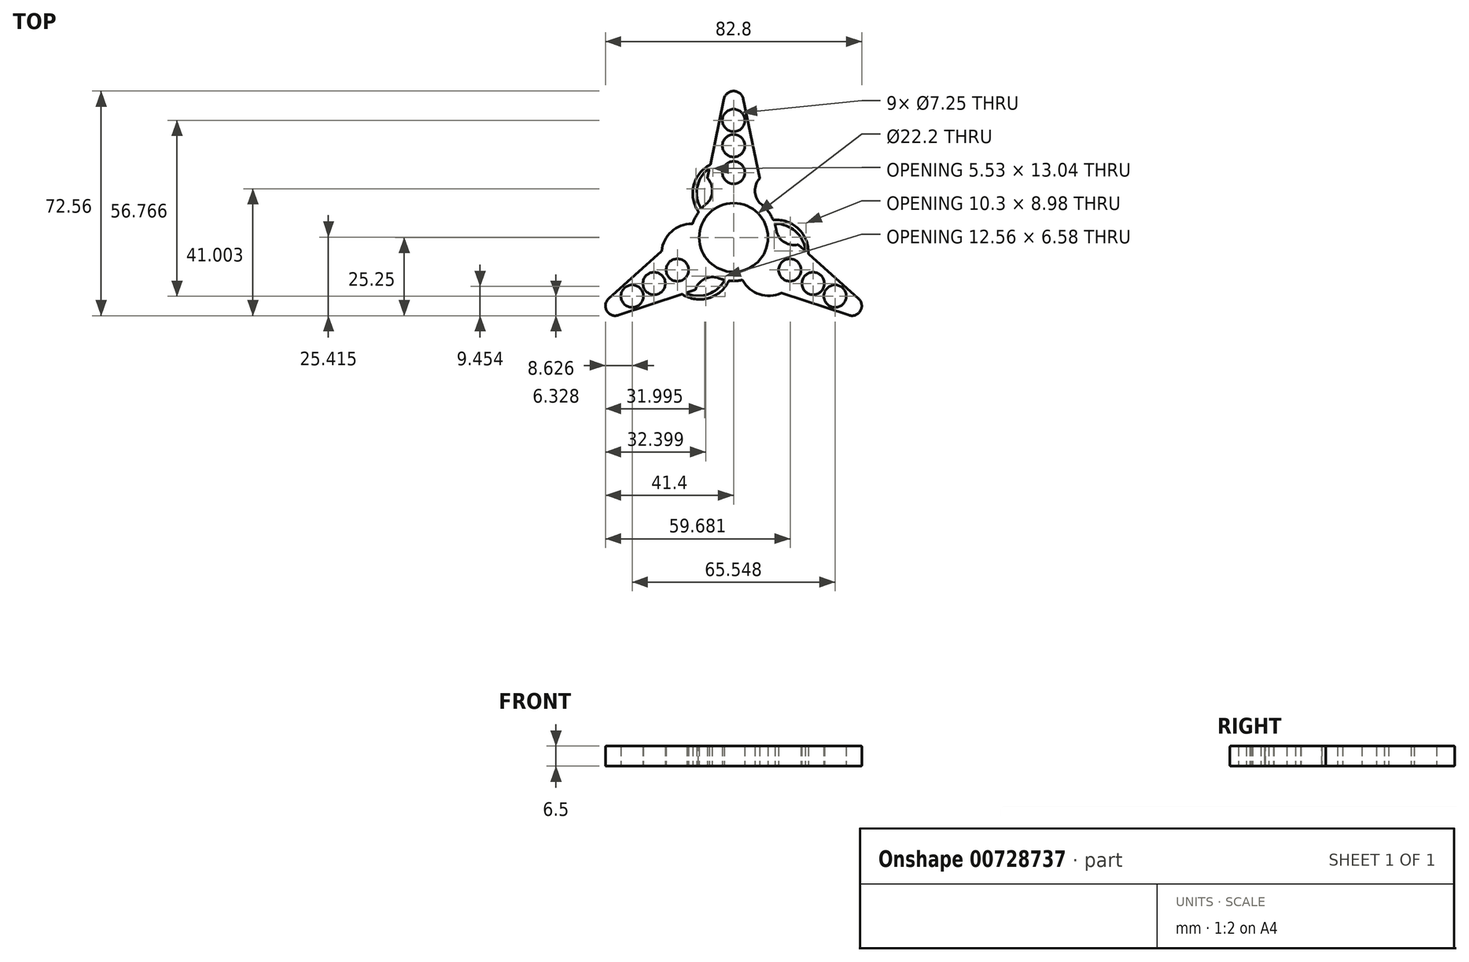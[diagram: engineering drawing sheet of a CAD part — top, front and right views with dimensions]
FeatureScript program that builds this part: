
annotation { "Feature Type Name" : "Feature", "Feature Type Description" : "" }
export const myFeature = defineFeature(function(context is Context, id is Id, definition is map)
    precondition{}
    {
        {
            var Q0;
            Q0=qCreatedBy(makeId("Top.planeOp"),FACE);
            var sketch = newSketch(context, id + "F0", { "sketchPlane" : qUnion([Q0])});
            skCircle(sketch, "E0", {"center": v(0, 0) * mm, "radius": 11.1 * mm});
            skCircle(sketch, "E1", {"center": v(0, 0) * mm, "radius": 14 * mm});
            skPoint(sketch, "E2", {"position": v(-8.44, 19.16) * mm});
            skPoint(sketch, "E3", {"position": v(-3.12, 44.77) * mm});
            skLineSegment(sketch, "E4", {"start": v(-8.44, 19.16) * mm, "end": v(-3.12, 44.77) * mm});
            skPoint(sketch, "E5.MirrorP", {"position": v(8.44, 19.16) * mm});
            skLineSegment(sketch, "E6.MirrorCS", {"start": v(8.44, 19.16) * mm, "end": v(3.12, 44.77) * mm});
            skPoint(sketch, "E7.MirrorP", {"position": v(3.12, 44.77) * mm});
            skArc(sketch, "E8", {"start": v(3.12, 44.77) * mm, "mid": v(0, 47.31) * mm, "end": v(-3.12, 44.77) * mm});
            skCircle(sketch, "E9", {"center": v(0, 37.84) * mm, "radius": 3.62 * mm});
            skCircle(sketch, "E10", {"center": v(0, 29.66) * mm, "radius": 3.62 * mm});
            skCircle(sketch, "E11", {"center": v(0, 20.98) * mm, "radius": 3.62 * mm});
            skLineSegment(sketch, "E12.1.0", {"start": v(-12.37, -16.89) * mm, "end": v(-37.21, -25.09) * mm});
            skArc(sketch, "E12.1.1", {"start": v(-40.33, -19.68) * mm, "mid": v(-40.97, -23.66) * mm, "end": v(-37.21, -25.09) * mm});
            skLineSegment(sketch, "E12.1.2", {"start": v(-20.81, -2.27) * mm, "end": v(-40.33, -19.68) * mm});
            skCircle(sketch, "E12.1.3", {"center": v(-32.77, -18.92) * mm, "radius": 3.62 * mm});
            skCircle(sketch, "E12.1.4", {"center": v(-25.68, -14.83) * mm, "radius": 3.62 * mm});
            skCircle(sketch, "E12.1.5", {"center": v(-18.17, -10.5) * mm, "radius": 3.62 * mm});
            skLineSegment(sketch, "E12.2.0", {"start": v(20.81, -2.27) * mm, "end": v(40.33, -19.68) * mm});
            skArc(sketch, "E12.2.1", {"start": v(37.21, -25.09) * mm, "mid": v(40.97, -23.66) * mm, "end": v(40.33, -19.68) * mm});
            skLineSegment(sketch, "E12.2.2", {"start": v(12.37, -16.89) * mm, "end": v(37.21, -25.09) * mm});
            skCircle(sketch, "E12.2.3", {"center": v(32.77, -18.92) * mm, "radius": 3.62 * mm});
            skCircle(sketch, "E12.2.4", {"center": v(25.68, -14.83) * mm, "radius": 3.62 * mm});
            skCircle(sketch, "E12.2.5", {"center": v(18.17, -10.5) * mm, "radius": 3.62 * mm});
            skArc(sketch, "E13", {"start": v(-8.44, 11.17) * mm, "mid": v(-6.9, 15.16) * mm, "end": v(-8.44, 19.16) * mm});
            skArc(sketch, "E14.MirrorCS", {"start": v(8.44, 11.17) * mm, "mid": v(6.9, 15.16) * mm, "end": v(8.44, 19.16) * mm});
            skArc(sketch, "E15.1.0", {"start": v(-5.45, -12.9) * mm, "mid": v(-9.69, -13.55) * mm, "end": v(-12.37, -16.89) * mm});
            skArc(sketch, "E15.1.1", {"start": v(-13.9, 1.73) * mm, "mid": v(-16.58, -1.61) * mm, "end": v(-20.81, -2.27) * mm});
            skArc(sketch, "E15.2.0", {"start": v(13.9, 1.73) * mm, "mid": v(16.58, -1.61) * mm, "end": v(20.81, -2.27) * mm});
            skArc(sketch, "E15.2.1", {"start": v(5.45, -12.9) * mm, "mid": v(9.69, -13.55) * mm, "end": v(12.37, -16.89) * mm});
            skArc(sketch, "E16", {"start": v(-7.77, 22.37) * mm, "mid": v(-11.72, 16.38) * mm, "end": v(-10.46, 9.31) * mm});
            skArc(sketch, "E17", {"start": v(-7.53, 23.55) * mm, "mid": v(-12.92, 16.77) * mm, "end": v(-11.3, 8.25) * mm});
            skArc(sketch, "E18.MirrorCS", {"start": v(7.53, 23.55) * mm, "mid": v(12.92, 16.77) * mm, "end": v(11.3, 8.25) * mm});
            skArc(sketch, "E19.MirrorCS", {"start": v(7.77, 22.37) * mm, "mid": v(11.72, 16.38) * mm, "end": v(10.46, 9.31) * mm});
            skArc(sketch, "E20.1.0", {"start": v(-16.63, -18.3) * mm, "mid": v(-8.06, -19.57) * mm, "end": v(-1.5, -13.92) * mm});
            skArc(sketch, "E20.1.1", {"start": v(-15.49, -17.92) * mm, "mid": v(-8.32, -18.34) * mm, "end": v(-2.84, -13.7) * mm});
            skArc(sketch, "E20.1.2", {"start": v(-23.26, -4.45) * mm, "mid": v(-20.04, 1.96) * mm, "end": v(-13.3, 4.4) * mm});
            skArc(sketch, "E20.1.3", {"start": v(-24.16, -5.25) * mm, "mid": v(-20.98, 2.8) * mm, "end": v(-12.8, 5.67) * mm});
            skArc(sketch, "E20.2.0", {"start": v(24.16, -5.25) * mm, "mid": v(20.98, 2.8) * mm, "end": v(12.8, 5.67) * mm});
            skArc(sketch, "E20.2.1", {"start": v(23.26, -4.45) * mm, "mid": v(20.04, 1.96) * mm, "end": v(13.3, 4.4) * mm});
            skArc(sketch, "E20.2.2", {"start": v(15.49, -17.92) * mm, "mid": v(8.32, -18.34) * mm, "end": v(2.84, -13.7) * mm});
            skArc(sketch, "E20.2.3", {"start": v(16.63, -18.3) * mm, "mid": v(8.06, -19.57) * mm, "end": v(1.5, -13.92) * mm});
            skSolve(sketch);
        }
        {
            var Q0;
            Q0=makeQuery(id+"F0.imprint","IMPRINT",FACE,{"disambiguationData":[TD([[makeQuery(id+"F0.imprint","IMPRINT",EDGE,{"derivedFrom":sQuery(id+"F0.wireOp",EDGE,"E4")}),-1.0]])]});
            var Q1;
            Q1=makeQuery(id+"F0.imprint","IMPRINT",FACE,{"disambiguationData":[TD([[makeQuery(id+"F0.imprint","IMPRINT",EDGE,{"derivedFrom":sQuery(id+"F0.wireOp",EDGE,"E12.1.0")}),-1.0]])]});
            var Q2;
            Q2=makeQuery(id+"F0.imprint","IMPRINT",FACE,{"disambiguationData":[TD([[makeQuery(id+"F0.imprint","IMPRINT",EDGE,{"derivedFrom":sQuery(id+"F0.wireOp",EDGE,"E12.2.0")}),-1.0]])]});
            var Q3;
            Q3=makeQuery(id+"F0.imprint","IMPRINT",FACE,{"disambiguationData":[TD([[makeQuery(id+"F0.imprint","IMPRINT",EDGE,{"derivedFrom":sQuery(id+"F0.wireOp",EDGE,"E0")}),-1.0]])]});
            var Q4;
            {var subQ0=sQuery(id+"F0.wireOp",EDGE,"E20.1.2");Q4=makeQuery(id+"F0.imprint","IMPRINT",FACE,{"disambiguationData":[TD([[makeQuery(id+"F0.imprint","IMPRINT",EDGE,{"derivedFrom":subQ0}),1.0]])]});}
            var Q5;
            {var subQ0=sQuery(id+"F0.wireOp",EDGE,"E16");Q5=makeQuery(id+"F0.imprint","IMPRINT",FACE,{"disambiguationData":[TD([[makeQuery(id+"F0.imprint","IMPRINT",EDGE,{"derivedFrom":subQ0}),-1.0]])]});}
            var Q6;
            {var subQ0=sQuery(id+"F0.wireOp",EDGE,"E18.MirrorCS");Q6=makeQuery(id+"F0.imprint","IMPRINT",FACE,{"disambiguationData":[TD([[makeQuery(id+"F0.imprint","IMPRINT",EDGE,{"derivedFrom":subQ0}),-1.0]])]});}
            var Q7;
            {var subQ0=sQuery(id+"F0.wireOp",EDGE,"E20.2.0");Q7=makeQuery(id+"F0.imprint","IMPRINT",FACE,{"disambiguationData":[TD([[makeQuery(id+"F0.imprint","IMPRINT",EDGE,{"derivedFrom":subQ0}),1.0]])]});}
            var Q8;
            {var subQ0=sQuery(id+"F0.wireOp",EDGE,"E20.2.2");Q8=makeQuery(id+"F0.imprint","IMPRINT",FACE,{"disambiguationData":[TD([[makeQuery(id+"F0.imprint","IMPRINT",EDGE,{"derivedFrom":subQ0}),1.0]])]});}
            var Q9;
            {var subQ0=sQuery(id+"F0.wireOp",EDGE,"E20.1.0");Q9=makeQuery(id+"F0.imprint","IMPRINT",FACE,{"disambiguationData":[TD([[makeQuery(id+"F0.imprint","IMPRINT",EDGE,{"derivedFrom":subQ0}),1.0]])]});}
            extrude(context, id + "F1", {"entities" : qUnion([Q0, Q1, Q2, Q3, Q4, Q5, Q6, Q7, Q8, Q9]), "depth" : 6.5 * mm, "offsetDistance" : 25 * mm});
        }
        {
            var Q0;
            Q0=makeQuery(id+"F1.opExtrude","SWEPT_FACE",FACE,{"disambiguationData":[OSD([sQuery(id+"F0.wireOp",EDGE,"E12.1.0")])]});
            var Q1;
            Q1=makeQuery(id+"F1.opExtrude","SWEPT_FACE",FACE,{"disambiguationData":[OSD([sQuery(id+"F0.wireOp",EDGE,"E12.1.5")])]});
            var Q2;
            Q2=makeQuery(id+"F1.opExtrude","SWEPT_FACE",FACE,{"disambiguationData":[OSD([sQuery(id+"F0.wireOp",EDGE,"E0")])]});
            var Q3;
            Q3=makeQuery(id+"F1.opExtrude","SWEPT_FACE",FACE,{"disambiguationData":[OSD([sQuery(id+"F0.wireOp",EDGE,"E12.1.2")])]});
            var Q4;
            Q4=makeQuery(id+"F1.opExtrude","SWEPT_FACE",FACE,{"disambiguationData":[OSD([sQuery(id+"F0.wireOp",EDGE,"E12.1.4")])]});
            var Q5;
            Q5=makeQuery(id+"F1.opExtrude","CAP_FACE",FACE,{"disambiguationData":[OSD([sQuery(id+"F0.wireOp",EDGE,"E0"),sQuery(id+"F0.wireOp",EDGE,"E1"),sQuery(id+"F0.wireOp",EDGE,"E4"),sQuery(id+"F0.wireOp",EDGE,"E6.MirrorCS"),sQuery(id+"F0.wireOp",EDGE,"E8"),sQuery(id+"F0.wireOp",EDGE,"E9"),sQuery(id+"F0.wireOp",EDGE,"E10"),sQuery(id+"F0.wireOp",EDGE,"E11"),sQuery(id+"F0.wireOp",EDGE,"E12.1.0"),sQuery(id+"F0.wireOp",EDGE,"E12.1.1"),sQuery(id+"F0.wireOp",EDGE,"E12.1.2"),sQuery(id+"F0.wireOp",EDGE,"E12.1.3"),sQuery(id+"F0.wireOp",EDGE,"E12.1.4"),sQuery(id+"F0.wireOp",EDGE,"E12.1.5"),sQuery(id+"F0.wireOp",EDGE,"E12.2.0"),sQuery(id+"F0.wireOp",EDGE,"E12.2.1"),sQuery(id+"F0.wireOp",EDGE,"E12.2.2"),sQuery(id+"F0.wireOp",EDGE,"E12.2.3"),sQuery(id+"F0.wireOp",EDGE,"E12.2.4"),sQuery(id+"F0.wireOp",EDGE,"E12.2.5"),sQuery(id+"F0.wireOp",EDGE,"E13"),sQuery(id+"F0.wireOp",EDGE,"E14.MirrorCS"),sQuery(id+"F0.wireOp",EDGE,"E15.1.0"),sQuery(id+"F0.wireOp",EDGE,"E15.1.1"),sQuery(id+"F0.wireOp",EDGE,"E15.2.0"),sQuery(id+"F0.wireOp",EDGE,"E15.2.1")])],"isStart":true});
            var Q6;
            Q6=makeQuery(id+"F1.opExtrude","SWEPT_FACE",FACE,{"disambiguationData":[OSD([sQuery(id+"F0.wireOp",EDGE,"E12.1.1")])]});
            var Q7;
            Q7=makeQuery(id+"F1.opExtrude","SWEPT_FACE",FACE,{"disambiguationData":[OSD([sQuery(id+"F0.wireOp",EDGE,"E15.2.1")])]});
            var Q8;
            Q8=makeQuery(id+"F1.opExtrude","SWEPT_FACE",FACE,{"disambiguationData":[OSD([sQuery(id+"F0.wireOp",EDGE,"E8")])]});
            var Q9;
            Q9=makeQuery(id+"F1.opExtrude","SWEPT_FACE",FACE,{"disambiguationData":[OSD([sQuery(id+"F0.wireOp",EDGE,"E6.MirrorCS")])]});
            var Q10;
            {var subQ0=sQuery(id+"F0.wireOp",EDGE,"E1");Q10=makeQuery(id+"F1.opExtrude","SWEPT_FACE",FACE,{"disambiguationData":[OSD([subQ0]),TDD([makeQuery(id+"F0.imprint","IMPRINT",EDGE,{"disambiguationData":[TD([[makeQuery(id+"F0.imprint","INTERSECT",VERTEX,{"derivedFrom":[subQ0,sQuery(id+"F0.wireOp",EDGE,"E15.1.0")]}),-1.0]])],"derivedFrom":subQ0})])]});}
            var Q11;
            Q11=makeQuery(id+"F1.opExtrude","SWEPT_FACE",FACE,{"disambiguationData":[OSD([sQuery(id+"F0.wireOp",EDGE,"E12.1.3")])]});
            var Q12;
            Q12=makeQuery(id+"F1.opExtrude","CAP_FACE",FACE,{"disambiguationData":[OSD([sQuery(id+"F0.wireOp",EDGE,"E0"),sQuery(id+"F0.wireOp",EDGE,"E1"),sQuery(id+"F0.wireOp",EDGE,"E4"),sQuery(id+"F0.wireOp",EDGE,"E6.MirrorCS"),sQuery(id+"F0.wireOp",EDGE,"E8"),sQuery(id+"F0.wireOp",EDGE,"E9"),sQuery(id+"F0.wireOp",EDGE,"E10"),sQuery(id+"F0.wireOp",EDGE,"E11"),sQuery(id+"F0.wireOp",EDGE,"E12.1.0"),sQuery(id+"F0.wireOp",EDGE,"E12.1.1"),sQuery(id+"F0.wireOp",EDGE,"E12.1.2"),sQuery(id+"F0.wireOp",EDGE,"E12.1.3"),sQuery(id+"F0.wireOp",EDGE,"E12.1.4"),sQuery(id+"F0.wireOp",EDGE,"E12.1.5"),sQuery(id+"F0.wireOp",EDGE,"E12.2.0"),sQuery(id+"F0.wireOp",EDGE,"E12.2.1"),sQuery(id+"F0.wireOp",EDGE,"E12.2.2"),sQuery(id+"F0.wireOp",EDGE,"E12.2.3"),sQuery(id+"F0.wireOp",EDGE,"E12.2.4"),sQuery(id+"F0.wireOp",EDGE,"E12.2.5"),sQuery(id+"F0.wireOp",EDGE,"E13"),sQuery(id+"F0.wireOp",EDGE,"E14.MirrorCS"),sQuery(id+"F0.wireOp",EDGE,"E15.1.0"),sQuery(id+"F0.wireOp",EDGE,"E15.1.1"),sQuery(id+"F0.wireOp",EDGE,"E15.2.0"),sQuery(id+"F0.wireOp",EDGE,"E15.2.1")])],"isStart":false});
            var Q13;
            Q13=makeQuery(id+"F1.opExtrude","SWEPT_FACE",FACE,{"disambiguationData":[OSD([sQuery(id+"F0.wireOp",EDGE,"E12.2.0")])]});
            var Q14;
            Q14=makeQuery(id+"F1.opExtrude","CAP_EDGE",EDGE,{"disambiguationData":[OSD([sQuery(id+"F0.wireOp",EDGE,"E0")])],"isStart":false});
            var Q15;
            Q15=makeQuery(id+"F1.opExtrude","CAP_EDGE",EDGE,{"disambiguationData":[OSD([sQuery(id+"F0.wireOp",EDGE,"E12.2.0")])],"isStart":false});
            var Q16;
            Q16=makeQuery(id+"F1.opExtrude","SWEPT_FACE",FACE,{"disambiguationData":[OSD([sQuery(id+"F0.wireOp",EDGE,"E12.2.1")])]});
            var Q17;
            Q17=makeQuery(id+"F1.opExtrude","SWEPT_FACE",FACE,{"disambiguationData":[OSD([sQuery(id+"F0.wireOp",EDGE,"E12.2.2")])]});
            var Q18;
            Q18=makeQuery(id+"F1.opExtrude","SWEPT_FACE",FACE,{"disambiguationData":[OSD([sQuery(id+"F0.wireOp",EDGE,"E12.2.3")])]});
            var Q19;
            Q19=makeQuery(id+"F1.opExtrude","CAP_EDGE",EDGE,{"disambiguationData":[OSD([sQuery(id+"F0.wireOp",EDGE,"E12.1.0")])],"isStart":true});
            var Q20;
            Q20=makeQuery(id+"F1.opExtrude","SWEPT_FACE",FACE,{"disambiguationData":[OSD([sQuery(id+"F0.wireOp",EDGE,"E12.2.4")])]});
            var Q21;
            Q21=makeQuery(id+"F1.opExtrude","CAP_EDGE",EDGE,{"disambiguationData":[OSD([sQuery(id+"F0.wireOp",EDGE,"E12.1.0")])],"isStart":false});
            var Q22;
            Q22=makeQuery(id+"F1.opExtrude","CAP_EDGE",EDGE,{"disambiguationData":[OSD([sQuery(id+"F0.wireOp",EDGE,"E12.2.2")])],"isStart":false});
            var Q23;
            Q23=makeQuery(id+"F1.opExtrude","SWEPT_FACE",FACE,{"disambiguationData":[OSD([sQuery(id+"F0.wireOp",EDGE,"E12.2.5")])]});
            var Q24;
            {var subQ0=sQuery(id+"F0.wireOp",EDGE,"E1");Q24=makeQuery(id+"F1.opExtrude","CAP_EDGE",EDGE,{"disambiguationData":[OSD([subQ0]),TDD([makeQuery(id+"F0.imprint","IMPRINT",EDGE,{"disambiguationData":[TD([[makeQuery(id+"F0.imprint","INTERSECT",VERTEX,{"derivedFrom":[subQ0,sQuery(id+"F0.wireOp",EDGE,"E15.1.0")]}),-1.0]])],"derivedFrom":subQ0})])],"isStart":true});}
            var Q25;
            {var subQ0=sQuery(id+"F0.wireOp",EDGE,"E1");Q25=makeQuery(id+"F1.opExtrude","CAP_EDGE",EDGE,{"disambiguationData":[OSD([subQ0]),TDD([makeQuery(id+"F0.imprint","IMPRINT",EDGE,{"disambiguationData":[TD([[makeQuery(id+"F0.imprint","INTERSECT",VERTEX,{"derivedFrom":[subQ0,sQuery(id+"F0.wireOp",EDGE,"E15.1.0")]}),-1.0]])],"derivedFrom":subQ0})])],"isStart":false});}
            var Q26;
            Q26=makeQuery(id+"F1.opExtrude","SWEPT_FACE",FACE,{"disambiguationData":[OSD([sQuery(id+"F0.wireOp",EDGE,"E15.1.0")])]});
            var Q27;
            Q27=makeQuery(id+"F1.opExtrude","CAP_EDGE",EDGE,{"disambiguationData":[OSD([sQuery(id+"F0.wireOp",EDGE,"E12.1.2")])],"isStart":false});
            var Q28;
            Q28=makeQuery(id+"F1.opExtrude","SWEPT_FACE",FACE,{"disambiguationData":[OSD([sQuery(id+"F0.wireOp",EDGE,"E15.1.1")])]});
            var Q29;
            Q29=makeQuery(id+"F1.opExtrude","SWEPT_FACE",FACE,{"disambiguationData":[OSD([sQuery(id+"F0.wireOp",EDGE,"E15.2.0")])]});
            var Q30;
            Q30=makeQuery(id+"F1.opExtrude","CAP_EDGE",EDGE,{"disambiguationData":[OSD([sQuery(id+"F0.wireOp",EDGE,"E8")])],"isStart":false});
            var Q31;
            Q31=makeQuery(id+"F1.opExtrude","CAP_EDGE",EDGE,{"disambiguationData":[OSD([sQuery(id+"F0.wireOp",EDGE,"E12.1.5")])],"isStart":true});
            var Q32;
            Q32=makeQuery(id+"F1.opExtrude","CAP_EDGE",EDGE,{"disambiguationData":[OSD([sQuery(id+"F0.wireOp",EDGE,"E12.1.5")])],"isStart":false});
            var Q33;
            Q33=makeQuery(id+"F1.opExtrude","SWEPT_EDGE",EDGE,{"disambiguationData":[OSD([sQuery(id+"F0.wireOp",EDGE,"E1"),sQuery(id+"F0.wireOp",EDGE,"E15.2.1")])]});
            var Q34;
            Q34=makeQuery(id+"F1.opExtrude","SWEPT_EDGE",EDGE,{"disambiguationData":[OSD([sQuery(id+"F0.wireOp",EDGE,"E4"),sQuery(id+"F0.wireOp",EDGE,"E8")])]});
            var Q35;
            Q35=makeQuery(id+"F1.opExtrude","CAP_EDGE",EDGE,{"disambiguationData":[OSD([sQuery(id+"F0.wireOp",EDGE,"E14.MirrorCS")])],"isStart":false});
            var Q36;
            Q36=makeQuery(id+"F1.opExtrude","CAP_EDGE",EDGE,{"disambiguationData":[OSD([sQuery(id+"F0.wireOp",EDGE,"E12.1.4")])],"isStart":false});
            var Q37;
            Q37=makeQuery(id+"F1.opExtrude","SWEPT_EDGE",EDGE,{"disambiguationData":[OSD([sQuery(id+"F0.wireOp",EDGE,"E1"),sQuery(id+"F0.wireOp",EDGE,"E15.1.0")])]});
            var Q38;
            Q38=makeQuery(id+"F1.opExtrude","CAP_EDGE",EDGE,{"disambiguationData":[OSD([sQuery(id+"F0.wireOp",EDGE,"E13")])],"isStart":false});
            var Q39;
            Q39=makeQuery(id+"F1.opExtrude","CAP_EDGE",EDGE,{"disambiguationData":[OSD([sQuery(id+"F0.wireOp",EDGE,"E12.1.4")])],"isStart":true});
            var Q40;
            Q40=makeQuery(id+"F1.opExtrude","CAP_EDGE",EDGE,{"disambiguationData":[OSD([sQuery(id+"F0.wireOp",EDGE,"E8")])],"isStart":true});
            var Q41;
            Q41=makeQuery(id+"F1.opExtrude","CAP_EDGE",EDGE,{"disambiguationData":[OSD([sQuery(id+"F0.wireOp",EDGE,"E12.2.5")])],"isStart":false});
            var Q42;
            Q42=makeQuery(id+"F1.opExtrude","CAP_EDGE",EDGE,{"disambiguationData":[OSD([sQuery(id+"F0.wireOp",EDGE,"E12.1.3")])],"isStart":false});
            var Q43;
            Q43=makeQuery(id+"F1.opExtrude","CAP_EDGE",EDGE,{"disambiguationData":[OSD([sQuery(id+"F0.wireOp",EDGE,"E6.MirrorCS")])],"isStart":false});
            var Q44;
            Q44=makeQuery(id+"F1.opExtrude","SWEPT_FACE",FACE,{"disambiguationData":[OSD([sQuery(id+"F0.wireOp",EDGE,"E11")])]});
            var Q45;
            Q45=makeQuery(id+"F1.opExtrude","SWEPT_EDGE",EDGE,{"disambiguationData":[OSD([sQuery(id+"F0.wireOp",EDGE,"E12.2.2"),sQuery(id+"F0.wireOp",EDGE,"E15.2.1")])]});
            var Q46;
            Q46=makeQuery(id+"F1.opExtrude","SWEPT_FACE",FACE,{"disambiguationData":[OSD([sQuery(id+"F0.wireOp",EDGE,"E10")])]});
            var Q47;
            Q47=makeQuery(id+"F1.opExtrude","SWEPT_EDGE",EDGE,{"disambiguationData":[OSD([sQuery(id+"F0.wireOp",EDGE,"E12.2.1"),sQuery(id+"F0.wireOp",EDGE,"E12.2.2")])]});
            var Q48;
            Q48=makeQuery(id+"F1.opExtrude","SWEPT_FACE",FACE,{"disambiguationData":[OSD([sQuery(id+"F0.wireOp",EDGE,"E9")])]});
            var Q49;
            Q49=makeQuery(id+"F1.opExtrude","SWEPT_EDGE",EDGE,{"disambiguationData":[OSD([sQuery(id+"F0.wireOp",EDGE,"E12.2.0"),sQuery(id+"F0.wireOp",EDGE,"E12.2.1")])]});
            var Q50;
            Q50=makeQuery(id+"F1.opExtrude","SWEPT_EDGE",EDGE,{"disambiguationData":[OSD([sQuery(id+"F0.wireOp",EDGE,"E12.2.0"),sQuery(id+"F0.wireOp",EDGE,"E15.2.0")])]});
            var Q51;
            Q51=makeQuery(id+"F1.opExtrude","SWEPT_EDGE",EDGE,{"disambiguationData":[OSD([sQuery(id+"F0.wireOp",EDGE,"E12.1.2"),sQuery(id+"F0.wireOp",EDGE,"E15.1.1")])]});
            var Q52;
            Q52=makeQuery(id+"F1.opExtrude","SWEPT_FACE",FACE,{"disambiguationData":[OSD([sQuery(id+"F0.wireOp",EDGE,"E4")])]});
            var Q53;
            Q53=makeQuery(id+"F1.opExtrude","SWEPT_EDGE",EDGE,{"disambiguationData":[OSD([sQuery(id+"F0.wireOp",EDGE,"E12.1.1"),sQuery(id+"F0.wireOp",EDGE,"E12.1.2")])]});
            var Q54;
            {var subQ0=sQuery(id+"F0.wireOp",EDGE,"E1");Q54=makeQuery(id+"F1.opExtrude","SWEPT_FACE",FACE,{"disambiguationData":[OSD([subQ0]),TDD([makeQuery(id+"F0.imprint","IMPRINT",EDGE,{"disambiguationData":[TD([[makeQuery(id+"F0.imprint","INTERSECT",VERTEX,{"derivedFrom":[subQ0,sQuery(id+"F0.wireOp",EDGE,"E13")]}),-1.0]])],"derivedFrom":subQ0})])]});}
            var Q55;
            Q55=makeQuery(id+"F1.opExtrude","SWEPT_EDGE",EDGE,{"disambiguationData":[OSD([sQuery(id+"F0.wireOp",EDGE,"E12.1.0"),sQuery(id+"F0.wireOp",EDGE,"E12.1.1")])]});
            var Q56;
            Q56=makeQuery(id+"F1.opExtrude","SWEPT_EDGE",EDGE,{"disambiguationData":[OSD([sQuery(id+"F0.wireOp",EDGE,"E12.1.0"),sQuery(id+"F0.wireOp",EDGE,"E15.1.0")])]});
            var Q57;
            {var subQ0=sQuery(id+"F0.wireOp",EDGE,"E1");Q57=makeQuery(id+"F1.opExtrude","SWEPT_FACE",FACE,{"disambiguationData":[OSD([subQ0]),TDD([makeQuery(id+"F0.imprint","IMPRINT",EDGE,{"disambiguationData":[TD([[makeQuery(id+"F0.imprint","INTERSECT",VERTEX,{"derivedFrom":[subQ0,sQuery(id+"F0.wireOp",EDGE,"E14.MirrorCS")]}),1.0]])],"derivedFrom":subQ0})])]});}
            var Q58;
            Q58=makeQuery(id+"F1.opExtrude","SWEPT_EDGE",EDGE,{"disambiguationData":[OSD([sQuery(id+"F0.wireOp",EDGE,"E6.MirrorCS"),sQuery(id+"F0.wireOp",EDGE,"E8")])]});
            var Q59;
            Q59=makeQuery(id+"F1.opExtrude","CAP_EDGE",EDGE,{"disambiguationData":[OSD([sQuery(id+"F0.wireOp",EDGE,"E0")])],"isStart":true});
            var Q60;
            Q60=makeQuery(id+"F1.opExtrude","CAP_EDGE",EDGE,{"disambiguationData":[OSD([sQuery(id+"F0.wireOp",EDGE,"E15.1.0")])],"isStart":true});
            var Q61;
            Q61=makeQuery(id+"F1.opExtrude","CAP_EDGE",EDGE,{"disambiguationData":[OSD([sQuery(id+"F0.wireOp",EDGE,"E12.2.0")])],"isStart":true});
            var Q62;
            Q62=makeQuery(id+"F1.opExtrude","CAP_EDGE",EDGE,{"disambiguationData":[OSD([sQuery(id+"F0.wireOp",EDGE,"E15.1.0")])],"isStart":false});
            var Q63;
            {var subQ0=sQuery(id+"F0.wireOp",EDGE,"E1");Q63=makeQuery(id+"F1.opExtrude","CAP_EDGE",EDGE,{"disambiguationData":[OSD([subQ0]),TDD([makeQuery(id+"F0.imprint","IMPRINT",EDGE,{"disambiguationData":[TD([[makeQuery(id+"F0.imprint","INTERSECT",VERTEX,{"derivedFrom":[subQ0,sQuery(id+"F0.wireOp",EDGE,"E14.MirrorCS")]}),1.0]])],"derivedFrom":subQ0})])],"isStart":true});}
            var Q64;
            Q64=makeQuery(id+"F1.opExtrude","CAP_EDGE",EDGE,{"disambiguationData":[OSD([sQuery(id+"F0.wireOp",EDGE,"E12.2.1")])],"isStart":true});
            var Q65;
            Q65=makeQuery(id+"F1.opExtrude","CAP_EDGE",EDGE,{"disambiguationData":[OSD([sQuery(id+"F0.wireOp",EDGE,"E15.1.1")])],"isStart":true});
            var Q66;
            {var subQ0=sQuery(id+"F0.wireOp",EDGE,"E1");Q66=makeQuery(id+"F1.opExtrude","CAP_EDGE",EDGE,{"disambiguationData":[OSD([subQ0]),TDD([makeQuery(id+"F0.imprint","IMPRINT",EDGE,{"disambiguationData":[TD([[makeQuery(id+"F0.imprint","INTERSECT",VERTEX,{"derivedFrom":[subQ0,sQuery(id+"F0.wireOp",EDGE,"E14.MirrorCS")]}),1.0]])],"derivedFrom":subQ0})])],"isStart":false});}
            var Q67;
            Q67=makeQuery(id+"F1.opExtrude","CAP_EDGE",EDGE,{"disambiguationData":[OSD([sQuery(id+"F0.wireOp",EDGE,"E12.2.1")])],"isStart":false});
            var Q68;
            Q68=makeQuery(id+"F1.opExtrude","CAP_EDGE",EDGE,{"disambiguationData":[OSD([sQuery(id+"F0.wireOp",EDGE,"E15.1.1")])],"isStart":false});
            var Q69;
            {var subQ0=sQuery(id+"F0.wireOp",EDGE,"E1");Q69=makeQuery(id+"F1.opExtrude","CAP_EDGE",EDGE,{"disambiguationData":[OSD([subQ0]),TDD([makeQuery(id+"F0.imprint","IMPRINT",EDGE,{"disambiguationData":[TD([[makeQuery(id+"F0.imprint","INTERSECT",VERTEX,{"derivedFrom":[subQ0,sQuery(id+"F0.wireOp",EDGE,"E13")]}),-1.0]])],"derivedFrom":subQ0})])],"isStart":true});}
            var Q70;
            Q70=makeQuery(id+"F1.opExtrude","CAP_EDGE",EDGE,{"disambiguationData":[OSD([sQuery(id+"F0.wireOp",EDGE,"E12.2.2")])],"isStart":true});
            var Q71;
            Q71=makeQuery(id+"F1.opExtrude","CAP_EDGE",EDGE,{"disambiguationData":[OSD([sQuery(id+"F0.wireOp",EDGE,"E15.2.0")])],"isStart":true});
            var Q72;
            {var subQ0=sQuery(id+"F0.wireOp",EDGE,"E1");Q72=makeQuery(id+"F1.opExtrude","CAP_EDGE",EDGE,{"disambiguationData":[OSD([subQ0]),TDD([makeQuery(id+"F0.imprint","IMPRINT",EDGE,{"disambiguationData":[TD([[makeQuery(id+"F0.imprint","INTERSECT",VERTEX,{"derivedFrom":[subQ0,sQuery(id+"F0.wireOp",EDGE,"E13")]}),-1.0]])],"derivedFrom":subQ0})])],"isStart":false});}
            var Q73;
            Q73=makeQuery(id+"F1.opExtrude","CAP_EDGE",EDGE,{"disambiguationData":[OSD([sQuery(id+"F0.wireOp",EDGE,"E15.2.0")])],"isStart":false});
            var Q74;
            Q74=makeQuery(id+"F1.opExtrude","CAP_EDGE",EDGE,{"disambiguationData":[OSD([sQuery(id+"F0.wireOp",EDGE,"E12.1.1")])],"isStart":true});
            var Q75;
            Q75=makeQuery(id+"F1.opExtrude","CAP_EDGE",EDGE,{"disambiguationData":[OSD([sQuery(id+"F0.wireOp",EDGE,"E12.2.3")])],"isStart":true});
            var Q76;
            Q76=makeQuery(id+"F1.opExtrude","CAP_EDGE",EDGE,{"disambiguationData":[OSD([sQuery(id+"F0.wireOp",EDGE,"E15.2.1")])],"isStart":true});
            var Q77;
            Q77=makeQuery(id+"F1.opExtrude","SWEPT_FACE",FACE,{"disambiguationData":[OSD([sQuery(id+"F0.wireOp",EDGE,"E13")])]});
            var Q78;
            Q78=makeQuery(id+"F1.opExtrude","CAP_EDGE",EDGE,{"disambiguationData":[OSD([sQuery(id+"F0.wireOp",EDGE,"E12.1.1")])],"isStart":false});
            var Q79;
            Q79=makeQuery(id+"F1.opExtrude","CAP_EDGE",EDGE,{"disambiguationData":[OSD([sQuery(id+"F0.wireOp",EDGE,"E12.2.3")])],"isStart":false});
            var Q80;
            Q80=makeQuery(id+"F1.opExtrude","CAP_EDGE",EDGE,{"disambiguationData":[OSD([sQuery(id+"F0.wireOp",EDGE,"E15.2.1")])],"isStart":false});
            var Q81;
            Q81=makeQuery(id+"F1.opExtrude","SWEPT_FACE",FACE,{"disambiguationData":[OSD([sQuery(id+"F0.wireOp",EDGE,"E14.MirrorCS")])]});
            var Q82;
            Q82=makeQuery(id+"F1.opExtrude","CAP_EDGE",EDGE,{"disambiguationData":[OSD([sQuery(id+"F0.wireOp",EDGE,"E4")])],"isStart":true});
            var Q83;
            Q83=makeQuery(id+"F1.opExtrude","CAP_EDGE",EDGE,{"disambiguationData":[OSD([sQuery(id+"F0.wireOp",EDGE,"E12.1.2")])],"isStart":true});
            var Q84;
            Q84=makeQuery(id+"F1.opExtrude","CAP_EDGE",EDGE,{"disambiguationData":[OSD([sQuery(id+"F0.wireOp",EDGE,"E12.2.4")])],"isStart":true});
            var Q85;
            Q85=makeQuery(id+"F1.opExtrude","CAP_EDGE",EDGE,{"disambiguationData":[OSD([sQuery(id+"F0.wireOp",EDGE,"E4")])],"isStart":false});
            var Q86;
            Q86=makeQuery(id+"F1.opExtrude","CAP_EDGE",EDGE,{"disambiguationData":[OSD([sQuery(id+"F0.wireOp",EDGE,"E12.2.4")])],"isStart":false});
            var Q87;
            Q87=makeQuery(id+"F1.opExtrude","CAP_EDGE",EDGE,{"disambiguationData":[OSD([sQuery(id+"F0.wireOp",EDGE,"E6.MirrorCS")])],"isStart":true});
            var Q88;
            Q88=makeQuery(id+"F1.opExtrude","CAP_EDGE",EDGE,{"disambiguationData":[OSD([sQuery(id+"F0.wireOp",EDGE,"E12.1.3")])],"isStart":true});
            var Q89;
            Q89=makeQuery(id+"F1.opExtrude","CAP_EDGE",EDGE,{"disambiguationData":[OSD([sQuery(id+"F0.wireOp",EDGE,"E12.2.5")])],"isStart":true});
            var Q90;
            Q90=makeQuery(id+"F1.opExtrude","CAP_EDGE",EDGE,{"disambiguationData":[OSD([sQuery(id+"F0.wireOp",EDGE,"E9")])],"isStart":false});
            var Q91;
            Q91=makeQuery(id+"F1.opExtrude","SWEPT_EDGE",EDGE,{"disambiguationData":[OSD([sQuery(id+"F0.wireOp",EDGE,"E1"),sQuery(id+"F0.wireOp",EDGE,"E15.1.1")])]});
            var Q92;
            Q92=makeQuery(id+"F1.opExtrude","SWEPT_EDGE",EDGE,{"disambiguationData":[OSD([sQuery(id+"F0.wireOp",EDGE,"E4"),sQuery(id+"F0.wireOp",EDGE,"E13")])]});
            var Q93;
            Q93=makeQuery(id+"F1.opExtrude","CAP_EDGE",EDGE,{"disambiguationData":[OSD([sQuery(id+"F0.wireOp",EDGE,"E14.MirrorCS")])],"isStart":true});
            var Q94;
            Q94=makeQuery(id+"F1.opExtrude","CAP_EDGE",EDGE,{"disambiguationData":[OSD([sQuery(id+"F0.wireOp",EDGE,"E9")])],"isStart":true});
            var Q95;
            Q95=makeQuery(id+"F1.opExtrude","SWEPT_EDGE",EDGE,{"disambiguationData":[OSD([sQuery(id+"F0.wireOp",EDGE,"E1"),sQuery(id+"F0.wireOp",EDGE,"E15.2.0")])]});
            var Q96;
            Q96=makeQuery(id+"F1.opExtrude","CAP_EDGE",EDGE,{"disambiguationData":[OSD([sQuery(id+"F0.wireOp",EDGE,"E13")])],"isStart":true});
            var Q97;
            Q97=makeQuery(id+"F1.opExtrude","SWEPT_EDGE",EDGE,{"disambiguationData":[OSD([sQuery(id+"F0.wireOp",EDGE,"E1"),sQuery(id+"F0.wireOp",EDGE,"E14.MirrorCS")])]});
            var Q98;
            Q98=makeQuery(id+"F1.opExtrude","SWEPT_EDGE",EDGE,{"disambiguationData":[OSD([sQuery(id+"F0.wireOp",EDGE,"E1"),sQuery(id+"F0.wireOp",EDGE,"E13")])]});
            var Q99;
            Q99=makeQuery(id+"F1.opExtrude","SWEPT_EDGE",EDGE,{"disambiguationData":[OSD([sQuery(id+"F0.wireOp",EDGE,"E6.MirrorCS"),sQuery(id+"F0.wireOp",EDGE,"E14.MirrorCS")])]});
            var Q100;
            Q100=makeQuery(id+"F1.opExtrude","CAP_EDGE",EDGE,{"disambiguationData":[OSD([sQuery(id+"F0.wireOp",EDGE,"E10")])],"isStart":true});
            var Q101;
            Q101=makeQuery(id+"F1.opExtrude","CAP_EDGE",EDGE,{"disambiguationData":[OSD([sQuery(id+"F0.wireOp",EDGE,"E10")])],"isStart":false});
            var Q102;
            Q102=makeQuery(id+"F1.opExtrude","CAP_EDGE",EDGE,{"disambiguationData":[OSD([sQuery(id+"F0.wireOp",EDGE,"E11")])],"isStart":true});
            var Q103;
            Q103=makeQuery(id+"F1.opExtrude","CAP_EDGE",EDGE,{"disambiguationData":[OSD([sQuery(id+"F0.wireOp",EDGE,"E11")])],"isStart":false});
            fillet(context, id + "F2", {"entities" : qUnion([Q0, Q1, Q2, Q3, Q4, Q5, Q6, Q7, Q8, Q9, Q10, Q11, Q12, Q13, Q14, Q15, Q16, Q17, Q18, Q19, Q20, Q21, Q22, Q23, Q24, Q25, Q26, Q27, Q28, Q29, Q30, Q31, Q32, Q33, Q34, Q35, Q36, Q37, Q38, Q39, Q40, Q41, Q42, Q43, Q44, Q45, Q46, Q47, Q48, Q49, Q50, Q51, Q52, Q53, Q54, Q55, Q56, Q57, Q58, Q59, Q60, Q61, Q62, Q63, Q64, Q65, Q66, Q67, Q68, Q69, Q70, Q71, Q72, Q73, Q74, Q75, Q76, Q77, Q78, Q79, Q80, Q81, Q82, Q83, Q84, Q85, Q86, Q87, Q88, Q89, Q90, Q91, Q92, Q93, Q94, Q95, Q96, Q97, Q98, Q99, Q100, Q101, Q102, Q103]), "radius" : 0.25 * mm, "tangentPropagation" : true, "allowEdgeOverflow" : false});
        }
    });
